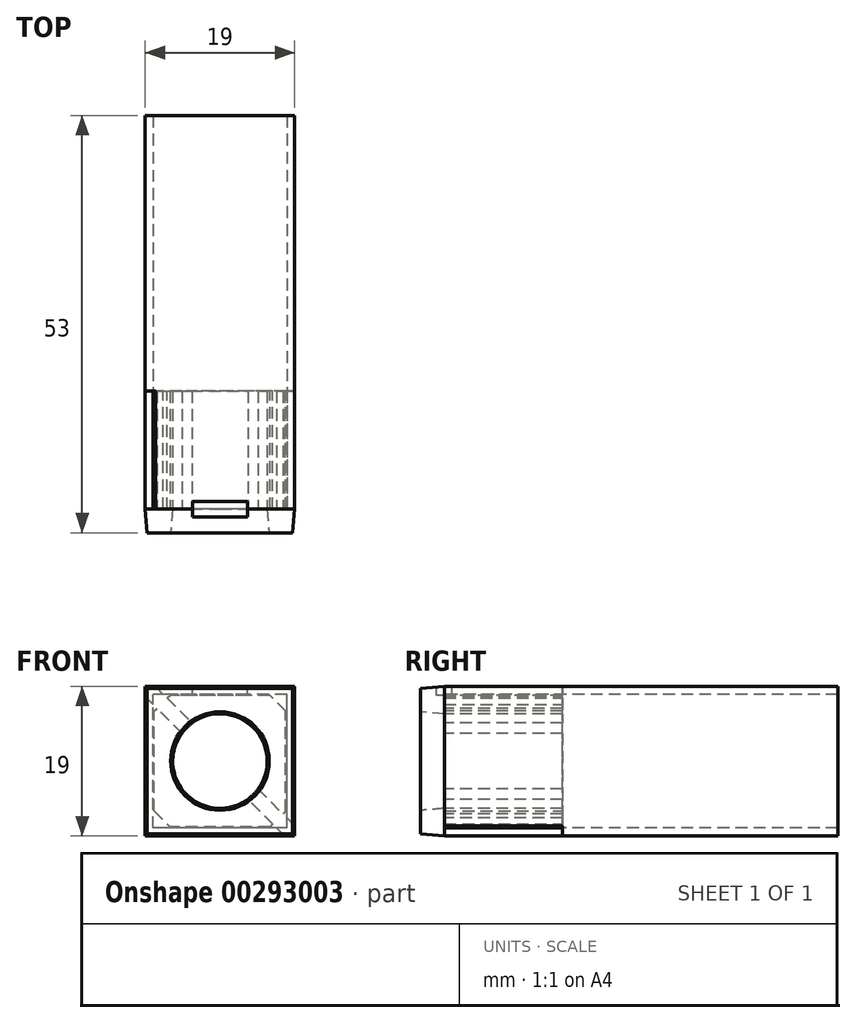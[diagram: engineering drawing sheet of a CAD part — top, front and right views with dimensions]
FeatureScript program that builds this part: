
annotation { "Feature Type Name" : "Feature", "Feature Type Description" : "" }
export const myFeature = defineFeature(function(context is Context, id is Id, definition is map)
    precondition{}
    {
        {
            var Q0;
            Q0=qCreatedBy(makeId("Front.planeOp"),FACE);
            var sketch = newSketch(context, id + "F0", { "sketchPlane" : qUnion([Q0])});
            skLineSegment(sketch, "E0.bottom", {"start": v(8.5, -8.5) * mm, "end": v(-8.5, -8.5) * mm});
            skLineSegment(sketch, "E0.top", {"start": v(8.5, 8.5) * mm, "end": v(-8.5, 8.5) * mm});
            skLineSegment(sketch, "E0.left", {"start": v(8.5, -8.5) * mm, "end": v(8.5, 8.5) * mm});
            skLineSegment(sketch, "E0.right", {"start": v(-8.5, -8.5) * mm, "end": v(-8.5, 8.5) * mm});
            skPoint(sketch, "E0.middle", {"position": v(0, 0) * mm});
            skLineSegment(sketch, "E1.0", {"start": v(9.5, 9.5) * mm, "end": v(-9.5, 9.5) * mm});
            skLineSegment(sketch, "E1.1", {"start": v(9.5, -9.5) * mm, "end": v(9.5, 9.5) * mm});
            skLineSegment(sketch, "E1.2", {"start": v(9.5, -9.5) * mm, "end": v(-9.5, -9.5) * mm});
            skLineSegment(sketch, "E1.3", {"start": v(-9.5, -9.5) * mm, "end": v(-9.5, 9.5) * mm});
            skSolve(sketch);
        }
        {
            var Q0;
            Q0 = qSketchRegion(id + "F0", true);
            extrude(context, id + "F1", {"entities" : qUnion([Q0]), "oppositeDirection" : true, "depth" : 50 * mm});
        }
        {
            var Q0;
            Q0=makeQuery(id+"F1.opExtrude","CAP_FACE",FACE,{"disambiguationData":[OSD([sQuery(id+"F0.wireOp",EDGE,"E0.bottom"),sQuery(id+"F0.wireOp",EDGE,"E0.top"),sQuery(id+"F0.wireOp",EDGE,"E0.left"),sQuery(id+"F0.wireOp",EDGE,"E0.right"),sQuery(id+"F0.wireOp",EDGE,"E1.0"),sQuery(id+"F0.wireOp",EDGE,"E1.1"),sQuery(id+"F0.wireOp",EDGE,"E1.2"),sQuery(id+"F0.wireOp",EDGE,"E1.3")])],"isStart":true});
            var sketch = newSketch(context, id + "F2", { "sketchPlane" : qUnion([Q0])});
            skLineSegment(sketch, "E2.0", {"start": v(8.35, 8.35) * mm, "end": v(-8.35, 8.35) * mm});
            skLineSegment(sketch, "E2.1", {"start": v(8.35, -8.35) * mm, "end": v(8.35, 8.35) * mm});
            skLineSegment(sketch, "E2.2", {"start": v(8.35, -8.35) * mm, "end": v(-8.35, -8.35) * mm});
            skLineSegment(sketch, "E2.3", {"start": v(-8.35, -8.35) * mm, "end": v(-8.35, 8.35) * mm});
            skCircle(sketch, "E3", {"center": v(0, 0) * mm, "radius": 6 * mm});
            skSolve(sketch);
        }
        {
            var Q0;
            Q0 = qSketchRegion(id + "F2", true);
            extrude(context, id + "F3", {"entities" : qUnion([Q0]), "oppositeDirection" : true, "depth" : 15 * mm});
        }
        {
            var Q0;
            Q0=makeQuery(id+"F3.opExtrude","CAP_FACE",FACE,{"disambiguationData":[OSD([sQuery(id+"F2.wireOp",EDGE,"E2.0"),sQuery(id+"F2.wireOp",EDGE,"E2.1"),sQuery(id+"F2.wireOp",EDGE,"E2.2"),sQuery(id+"F2.wireOp",EDGE,"E2.3"),sQuery(id+"F2.wireOp",EDGE,"E3")])],"isStart":true});
            var sketch = newSketch(context, id + "F4", { "sketchPlane" : qUnion([Q0])});
            skLineSegment(sketch, "E4.0.0", {"start": v(-9.5, 9.5) * mm, "end": v(-9.5, -9.5) * mm});
            skLineSegment(sketch, "E4.0.1", {"start": v(-9.5, -9.5) * mm, "end": v(9.5, -9.5) * mm});
            skLineSegment(sketch, "E4.0.2", {"start": v(9.5, -9.5) * mm, "end": v(9.5, 9.5) * mm});
            skLineSegment(sketch, "E4.0.3", {"start": v(9.5, 9.5) * mm, "end": v(-9.5, 9.5) * mm});
            skCircle(sketch, "E5.0", {"center": v(0, 0) * mm, "radius": 6 * mm});
            skSolve(sketch);
        }
        {
            var Q0;
            Q0 = qSketchRegion(id + "F4", true);
            extrude(context, id + "F5", {"entities" : qUnion([Q0]), "operationType" : NewBodyOperationType.ADD, "depth" : 3 * mm, "hasDraft" : true, "draftAngle" : 5 * degree, "draftPullDirection" : true});
        }
        {
            var Q0;
            Q0=makeQuery(id+"F1.opExtrude","SWEPT_FACE",FACE,{"disambiguationData":[OSD([sQuery(id+"F0.wireOp",EDGE,"E1.0")])]});
            var sketch = newSketch(context, id + "F6", { "sketchPlane" : qUnion([Q0])});
            skLineSegment(sketch, "E6.bottom", {"start": v(3.5, 1) * mm, "end": v(-3.5, 1) * mm});
            skLineSegment(sketch, "E6.top", {"start": v(3.5, -1) * mm, "end": v(-3.5, -1) * mm});
            skLineSegment(sketch, "E6.left", {"start": v(3.5, 1) * mm, "end": v(3.5, -1) * mm});
            skLineSegment(sketch, "E6.right", {"start": v(-3.5, 1) * mm, "end": v(-3.5, -1) * mm});
            skPoint(sketch, "E6.middle", {"position": v(0, 0) * mm});
            skSolve(sketch);
        }
        {
            var Q0;
            {var subQ0=sQuery(id+"F6.wireOp",EDGE,"E6.top");Q0=makeQuery(id+"F6.imprint","IMPRINT",FACE,{"disambiguationData":[TD([[makeQuery(id+"F6.imprint","IMPRINT",EDGE,{"derivedFrom":subQ0}),-1.0]])]});}
            var Q1;
            {var subQ0=sQuery(id+"F6.wireOp",EDGE,"E6.bottom");Q1=makeQuery(id+"F6.imprint","IMPRINT",FACE,{"disambiguationData":[TD([[makeQuery(id+"F6.imprint","IMPRINT",EDGE,{"derivedFrom":subQ0}),1.0]])]});}
            var Q2;
            Q2=makeQuery(id+"F3.opExtrude","SWEPT_FACE",FACE,{"disambiguationData":[OSD([sQuery(id+"F2.wireOp",EDGE,"E2.0")])]});
            extrude(context, id + "F7", {"entities" : qUnion([Q0, Q1]), "operationType" : NewBodyOperationType.REMOVE, "oppositeDirection" : true, "endBoundEntityFace" : qUnion([Q2]), "depth" : 1.15 * mm});
        }
        {
            var Q0;
            Q0=makeQuery(id+"F3.opExtrude","SWEPT_EDGE",EDGE,{"disambiguationData":[OSD([sQuery(id+"F2.wireOp",EDGE,"E2.0"),sQuery(id+"F2.wireOp",EDGE,"E2.1")])]});
            var Q1;
            Q1=makeQuery(id+"F3.opExtrude","SWEPT_EDGE",EDGE,{"disambiguationData":[OSD([sQuery(id+"F2.wireOp",EDGE,"E2.1"),sQuery(id+"F2.wireOp",EDGE,"E2.2")])]});
            var Q2;
            Q2=makeQuery(id+"F3.opExtrude","SWEPT_EDGE",EDGE,{"disambiguationData":[OSD([sQuery(id+"F2.wireOp",EDGE,"E2.2"),sQuery(id+"F2.wireOp",EDGE,"E2.3")])]});
            var Q3;
            Q3=makeQuery(id+"F3.opExtrude","SWEPT_EDGE",EDGE,{"disambiguationData":[OSD([sQuery(id+"F2.wireOp",EDGE,"E2.0"),sQuery(id+"F2.wireOp",EDGE,"E2.3")])]});
            chamfer(context, id + "F8", {"entities" : qUnion([Q0, Q1, Q2, Q3]), "width" : 2 * mm, "tangentPropagation" : true});
        }
        {
            var Q0;
            Q0=makeQuery(id+"F3.opExtrude","CAP_FACE",FACE,{"disambiguationData":[OSD([sQuery(id+"F2.wireOp",EDGE,"E2.0"),sQuery(id+"F2.wireOp",EDGE,"E2.1"),sQuery(id+"F2.wireOp",EDGE,"E2.2"),sQuery(id+"F2.wireOp",EDGE,"E2.3"),sQuery(id+"F2.wireOp",EDGE,"E3")])],"isStart":false});
            var sketch = newSketch(context, id + "F9", { "sketchPlane" : qUnion([Q0])});
            skLineSegment(sketch, "E7", {"start": v(12.79, 14.79) * mm, "end": v(-12.4, -10.4) * mm});
            skLineSegment(sketch, "E8", {"start": v(-12.4, -10.4) * mm, "end": v(-10.4, -12.4) * mm});
            skLineSegment(sketch, "E9", {"start": v(-10.4, -12.4) * mm, "end": v(14.65, 12.65) * mm});
            skLineSegment(sketch, "E10", {"start": v(14.65, 12.65) * mm, "end": v(12.79, 14.79) * mm});
            skLineSegment(sketch, "E11.0", {"start": v(12.76, 14.06) * mm, "end": v(-11.7, -10.4) * mm});
            skLineSegment(sketch, "E11.1", {"start": v(13.97, 12.67) * mm, "end": v(12.76, 14.06) * mm});
            skLineSegment(sketch, "E11.2", {"start": v(-10.4, -11.7) * mm, "end": v(13.97, 12.67) * mm});
            skLineSegment(sketch, "E11.3", {"start": v(-11.7, -10.4) * mm, "end": v(-10.4, -11.7) * mm});
            skSolve(sketch);
        }
        {
            var Q0;
            {var subQ0=sQuery(id+"F9.wireOp",EDGE,"E11.1");Q0=makeQuery(id+"F9.imprint","IMPRINT",FACE,{"disambiguationData":[TD([[makeQuery(id+"F9.imprint","IMPRINT",EDGE,{"derivedFrom":subQ0}),1.0]])]});}
            var Q1;
            {var subQ0=sQuery(id+"F9.wireOp",EDGE,"E11.0");var subQ1=sQuery(id+"F2.wireOp",EDGE,"E3");var subQ6=makeQuery(id+"F3.opExtrude","CAP_EDGE",EDGE,{"disambiguationData":[OSD([subQ1])],"isStart":false});var subQ7=makeQuery(id+"F9.imprint","INTERSECT",VERTEX,{"disambiguationData":[OD(0.0)],"derivedFrom":[subQ6,subQ0]});Q1=makeQuery(id+"F9.imprint","IMPRINT",FACE,{"disambiguationData":[TD([[makeQuery(id+"F9.imprint","IMPRINT",EDGE,{"disambiguationData":[TD([[subQ7,-1.0]])],"derivedFrom":subQ6}),1.0]])]});}
            var Q2;
            {var subQ0=sQuery(id+"F9.wireOp",EDGE,"E11.3");Q2=makeQuery(id+"F9.imprint","IMPRINT",FACE,{"disambiguationData":[TD([[makeQuery(id+"F9.imprint","IMPRINT",EDGE,{"derivedFrom":subQ0}),1.0]])]});}
            var Q3;
            {var subQ0=sQuery(id+"F9.wireOp",EDGE,"E11.0");var subQ1=makeQuery(id+"F3.opExtrude","CAP_EDGE",EDGE,{"disambiguationData":[OSD([sQuery(id+"F2.wireOp",EDGE,"E3")])],"isStart":false});var subQ2=makeQuery(id+"F9.imprint","INTERSECT",VERTEX,{"disambiguationData":[OD(0.0)],"derivedFrom":[subQ1,subQ0]});Q3=makeQuery(id+"F9.imprint","IMPRINT",FACE,{"disambiguationData":[TD([[makeQuery(id+"F9.imprint","IMPRINT",EDGE,{"disambiguationData":[TD([[subQ2,-1.0]])],"derivedFrom":subQ0}),1.0]])]});}
            var Q4;
            {var subQ0=sQuery(id+"F9.wireOp",EDGE,"E11.0");var subQ1=sQuery(id+"F2.wireOp",EDGE,"E3");var subQ2=makeQuery(id+"F3.opExtrude","CAP_EDGE",EDGE,{"disambiguationData":[OSD([subQ1])],"isStart":false});var subQ3=makeQuery(id+"F9.imprint","INTERSECT",VERTEX,{"disambiguationData":[OD(1.0)],"derivedFrom":[subQ2,subQ0]});Q4=makeQuery(id+"F9.imprint","IMPRINT",FACE,{"disambiguationData":[TD([[makeQuery(id+"F9.imprint","IMPRINT",EDGE,{"disambiguationData":[TD([[subQ3,1.0]])],"derivedFrom":subQ2}),1.0]])]});}
            var Q5;
            {var subQ0=sQuery(id+"F4.wireOp",EDGE,"E4.0.3");var subQ2=sQuery(id+"F4.wireOp",EDGE,"E4.0.0");var subQ5=makeQuery(id+"F3.opExtrude","SWEPT_FACE",FACE,{"disambiguationData":[OSD([sQuery(id+"F2.wireOp",EDGE,"E2.0")])]});var subQ12=makeQuery(id+"F3.opExtrude","SWEPT_FACE",FACE,{"disambiguationData":[OSD([sQuery(id+"F2.wireOp",EDGE,"E2.2")])]});var subQ13=sQuery(id+"F4.wireOp",EDGE,"E4.0.1");var subQ15=sQuery(id+"F4.wireOp",EDGE,"E4.0.2");Q5=makeQuery(id+"FJbmcXwFBvmhBgo_2.3.F7.boolean.opBoolean","SPLIT",FACE,{"disambiguationData":[TD([subQ5])],"derivedFrom":makeQuery(id+"FJbmcXwFBvmhBgo_2.2.F7.boolean.opBoolean","SPLIT",FACE,{"disambiguationData":[TD([subQ5])],"derivedFrom":makeQuery(id+"FJbmcXwFBvmhBgo_2.1.F7.boolean.opBoolean","SPLIT",FACE,{"disambiguationData":[TD([subQ12])],"derivedFrom":makeQuery(id+"F5.opExtrude","CAP_FACE",FACE,{"disambiguationData":[OSD([subQ2,subQ13,subQ15,subQ0,sQuery(id+"F4.wireOp",EDGE,"E5.0")])],"isStart":true})})})});}
            extrude(context, id + "F10", {"entities" : qUnion([Q0, Q1, Q2, Q3, Q4]), "operationType" : NewBodyOperationType.REMOVE, "endBound" : BoundingType.UP_TO_SURFACE, "oppositeDirection" : true, "endBoundEntityFace" : qUnion([Q5]), "depth" : 25 * mm});
        }
    });
